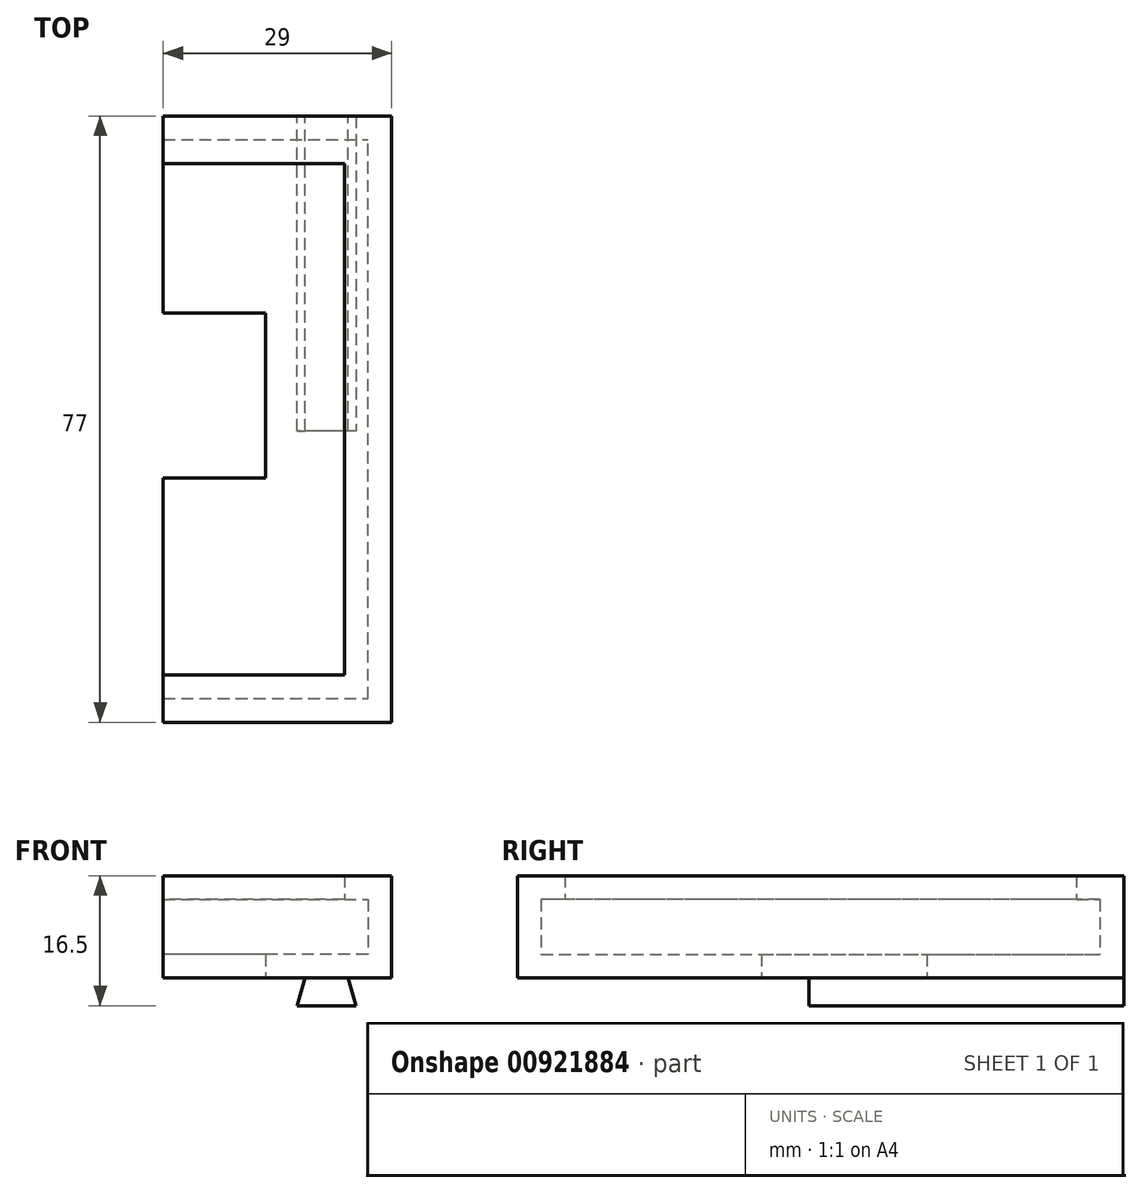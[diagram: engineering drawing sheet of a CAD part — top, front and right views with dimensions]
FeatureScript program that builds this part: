
annotation { "Feature Type Name" : "Feature", "Feature Type Description" : "" }
export const myFeature = defineFeature(function(context is Context, id is Id, definition is map)
    precondition{}
    {
        {
            var Q0;
            Q0=qCreatedBy(makeId("Top.planeOp"),FACE);
            var sketch = newSketch(context, id + "F0", { "sketchPlane" : qUnion([Q0])});
            skLineSegment(sketch, "E0", {"start": v(0, 0) * mm, "end": v(0, 31) * mm});
            skLineSegment(sketch, "E1", {"start": v(0, 31) * mm, "end": v(13, 31) * mm});
            skLineSegment(sketch, "E2", {"start": v(13, 31) * mm, "end": v(13, 52) * mm});
            skLineSegment(sketch, "E3", {"start": v(13, 52) * mm, "end": v(0, 52) * mm});
            skLineSegment(sketch, "E4", {"start": v(0, 52) * mm, "end": v(0, 77) * mm});
            skLineSegment(sketch, "E5", {"start": v(0, 77) * mm, "end": v(29, 77) * mm});
            skLineSegment(sketch, "E6", {"start": v(29, 77) * mm, "end": v(29, 0) * mm});
            skLineSegment(sketch, "E7", {"start": v(29, 0) * mm, "end": v(0, 0) * mm});
            skSolve(sketch);
        }
        {
            var Q0;
            Q0 = qSketchRegion(id + "F0", true);
            var Q1;
            Q1=makeQuery(id+"F0.imprint","IMPRINT",FACE,{"disambiguationData":[TD([[makeQuery(id+"F0.imprint","IMPRINT",EDGE,{"derivedFrom":sQuery(id+"F0.wireOp",EDGE,"E0")}),-1.0]])]});
            extrude(context, id + "F1", {"entities" : qUnion([Q0, Q1]), "depth" : 3 * mm, "offsetDistance" : 25 * mm});
        }
        {
            var Q0;
            Q0=makeQuery(id+"F1.opExtrude","CAP_FACE",FACE,{"disambiguationData":[OSD([sQuery(id+"F0.wireOp",EDGE,"E0"),sQuery(id+"F0.wireOp",EDGE,"E1"),sQuery(id+"F0.wireOp",EDGE,"E2"),sQuery(id+"F0.wireOp",EDGE,"E3"),sQuery(id+"F0.wireOp",EDGE,"E4"),sQuery(id+"F0.wireOp",EDGE,"E5"),sQuery(id+"F0.wireOp",EDGE,"E6"),sQuery(id+"F0.wireOp",EDGE,"E7")])],"isStart":false});
            var sketch = newSketch(context, id + "F2", { "sketchPlane" : qUnion([Q0])});
            skLineSegment(sketch, "E8", {"start": v(0, 3) * mm, "end": v(26, 3) * mm});
            skLineSegment(sketch, "E9", {"start": v(26, 3) * mm, "end": v(26, 74) * mm});
            skLineSegment(sketch, "E10", {"start": v(26, 74) * mm, "end": v(0, 74) * mm});
            skSolve(sketch);
        }
        {
            var Q0;
            Q0 = qSketchRegion(id + "F2", true);
            var Q1;
            {var subQ3=sQuery(id+"F2.wireOp",EDGE,"E8");Q1=makeQuery(id+"F2.imprint","IMPRINT",FACE,{"disambiguationData":[TD([[makeQuery(id+"F2.imprint","IMPRINT",EDGE,{"derivedFrom":subQ3}),-1.0]])]});}
            extrude(context, id + "F3", {"entities" : qUnion([Q0, Q1]), "operationType" : NewBodyOperationType.ADD, "depth" : 10 * mm, "offsetDistance" : 25 * mm});
        }
        {
            var Q0;
            Q0=makeQuery(id+"F3.opExtrude","SWEPT_FACE",FACE,{"disambiguationData":[OSD([sQuery(id+"F2.wireOp",EDGE,"E9")])]});
            var sketch = newSketch(context, id + "F4", { "sketchPlane" : qUnion([Q0])});
            skLineSegment(sketch, "E11", {"start": v(-74, 10) * mm, "end": v(-3, 10) * mm});
            skSolve(sketch);
        }
        {
            var Q0;
            Q0 = qSketchRegion(id + "F4", true);
            var Q1;
            {var subQ0=sQuery(id+"F4.wireOp",EDGE,"E11");Q1=makeQuery(id+"F4.imprint","IMPRINT",FACE,{"disambiguationData":[TD([[makeQuery(id+"F4.imprint","IMPRINT",EDGE,{"derivedFrom":subQ0}),1.0]])]});}
            extrude(context, id + "F5", {"entities" : qUnion([Q0, Q1]), "operationType" : NewBodyOperationType.ADD, "depth" : 3 * mm, "offsetDistance" : 25 * mm});
        }
        {
            var Q0;
            Q0=makeQuery(id+"F3.opExtrude","SWEPT_FACE",FACE,{"disambiguationData":[OSD([sQuery(id+"F2.wireOp",EDGE,"E10")])]});
            var sketch = newSketch(context, id + "F6", { "sketchPlane" : qUnion([Q0])});
            skLineSegment(sketch, "E12", {"start": v(23, 10) * mm, "end": v(0, 10) * mm});
            skSolve(sketch);
        }
        {
            var Q0;
            Q0 = qSketchRegion(id + "F6", true);
            var Q1;
            {var subQ0=sQuery(id+"F6.wireOp",EDGE,"E12");Q1=makeQuery(id+"F6.imprint","IMPRINT",FACE,{"disambiguationData":[TD([[makeQuery(id+"F6.imprint","IMPRINT",EDGE,{"derivedFrom":subQ0}),-1.0]])]});}
            extrude(context, id + "F7", {"entities" : qUnion([Q0, Q1]), "operationType" : NewBodyOperationType.ADD, "depth" : 3 * mm, "offsetDistance" : 25 * mm});
        }
        {
            var Q0;
            Q0=makeQuery(id+"F3.opExtrude","SWEPT_FACE",FACE,{"disambiguationData":[OSD([sQuery(id+"F2.wireOp",EDGE,"E8")])]});
            var sketch = newSketch(context, id + "F8", { "sketchPlane" : qUnion([Q0])});
            skLineSegment(sketch, "E13", {"start": v(-23, 10) * mm, "end": v(0, 10) * mm});
            skSolve(sketch);
        }
        {
            var Q0;
            Q0 = qSketchRegion(id + "F8", true);
            var Q1;
            {var subQ0=sQuery(id+"F8.wireOp",EDGE,"E13");Q1=makeQuery(id+"F8.imprint","IMPRINT",FACE,{"disambiguationData":[TD([[makeQuery(id+"F8.imprint","IMPRINT",EDGE,{"derivedFrom":subQ0}),1.0]])]});}
            extrude(context, id + "F9", {"entities" : qUnion([Q0, Q1]), "operationType" : NewBodyOperationType.ADD, "depth" : 3 * mm, "offsetDistance" : 25 * mm});
        }
        {
            var Q0;
            Q0=makeQuery(id+"F1.opExtrude","CAP_FACE",FACE,{"disambiguationData":[OSD([sQuery(id+"F0.wireOp",EDGE,"E0"),sQuery(id+"F0.wireOp",EDGE,"E1"),sQuery(id+"F0.wireOp",EDGE,"E2"),sQuery(id+"F0.wireOp",EDGE,"E3"),sQuery(id+"F0.wireOp",EDGE,"E4"),sQuery(id+"F0.wireOp",EDGE,"E5"),sQuery(id+"F0.wireOp",EDGE,"E6"),sQuery(id+"F0.wireOp",EDGE,"E7")])],"isStart":true});
            var sketch = newSketch(context, id + "F10", { "sketchPlane" : qUnion([Q0])});
            skLineSegment(sketch, "E14", {"start": v(24.5, -77) * mm, "end": v(24.5, -37) * mm});
            skLineSegment(sketch, "E15", {"start": v(24.5, -37) * mm, "end": v(17, -37) * mm});
            skLineSegment(sketch, "E16", {"start": v(17, -37) * mm, "end": v(17, -77) * mm});
            skSolve(sketch);
        }
        {
            var Q0;
            Q0 = qSketchRegion(id + "F10", true);
            var Q1;
            {var subQ0=sQuery(id+"F10.wireOp",EDGE,"E14");Q1=makeQuery(id+"F10.imprint","IMPRINT",FACE,{"disambiguationData":[TD([[makeQuery(id+"F10.imprint","IMPRINT",EDGE,{"derivedFrom":subQ0}),1.0]])]});}
            extrude(context, id + "F11", {"entities" : qUnion([Q0, Q1]), "operationType" : NewBodyOperationType.ADD, "depth" : 3.5 * mm, "offsetDistance" : 25 * mm});
        }
        {
            var Q0;
            {var subQ0=sQuery(id+"F0.wireOp",EDGE,"E5");Q0=makeQuery(id+"F11.boolean.opBoolean","MERGE",FACE,{"derivedFrom":[makeQuery(id+"F3.boolean.opBoolean","MERGE",FACE,{"derivedFrom":[makeQuery(id+"F1.opExtrude","SWEPT_FACE",FACE,{"disambiguationData":[OSD([subQ0])]}),makeQuery(id+"F3.opExtrude","SWEPT_FACE",FACE,{"disambiguationData":[OSD([subQ0])]})]}),makeQuery(id+"F11.opExtrude","SWEPT_FACE",FACE,{"disambiguationData":[OSD([subQ0])]})]});}
            var sketch = newSketch(context, id + "F12", { "sketchPlane" : qUnion([Q0])});
            skLineSegment(sketch, "E17", {"start": v(-24.5, -3.5) * mm, "end": v(-23.5, 0) * mm});
            skLineSegment(sketch, "E18", {"start": v(-23.5, 0) * mm, "end": v(-24.5, 0) * mm});
            skLineSegment(sketch, "E19", {"start": v(-17, -3.5) * mm, "end": v(-18, 0) * mm});
            skLineSegment(sketch, "E20", {"start": v(-18, 0) * mm, "end": v(-17, 0) * mm});
            skSolve(sketch);
        }
        {
            var Q0;
            Q0 = qSketchRegion(id + "F12", true);
            var Q1;
            Q1=makeQuery(id+"F12.imprint","IMPRINT",FACE,{"disambiguationData":[TD([[makeQuery(id+"F12.imprint","IMPRINT",EDGE,{"derivedFrom":sQuery(id+"F12.wireOp",EDGE,"E17")}),1.0]])]});
            extrude(context, id + "F13", {"entities" : qUnion([Q0, Q1]), "operationType" : NewBodyOperationType.REMOVE, "oppositeDirection" : true, "depth" : 40 * mm, "offsetDistance" : 25 * mm});
        }
        {
            var Q0;
            Q0=makeQuery(id+"F12.imprint","IMPRINT",FACE,{"disambiguationData":[TD([[makeQuery(id+"F12.imprint","IMPRINT",EDGE,{"derivedFrom":sQuery(id+"F12.wireOp",EDGE,"E19")}),-1.0]])]});
            extrude(context, id + "F14", {"entities" : qUnion([Q0]), "operationType" : NewBodyOperationType.REMOVE, "oppositeDirection" : true, "depth" : 40 * mm, "offsetDistance" : 25 * mm});
        }
    });
